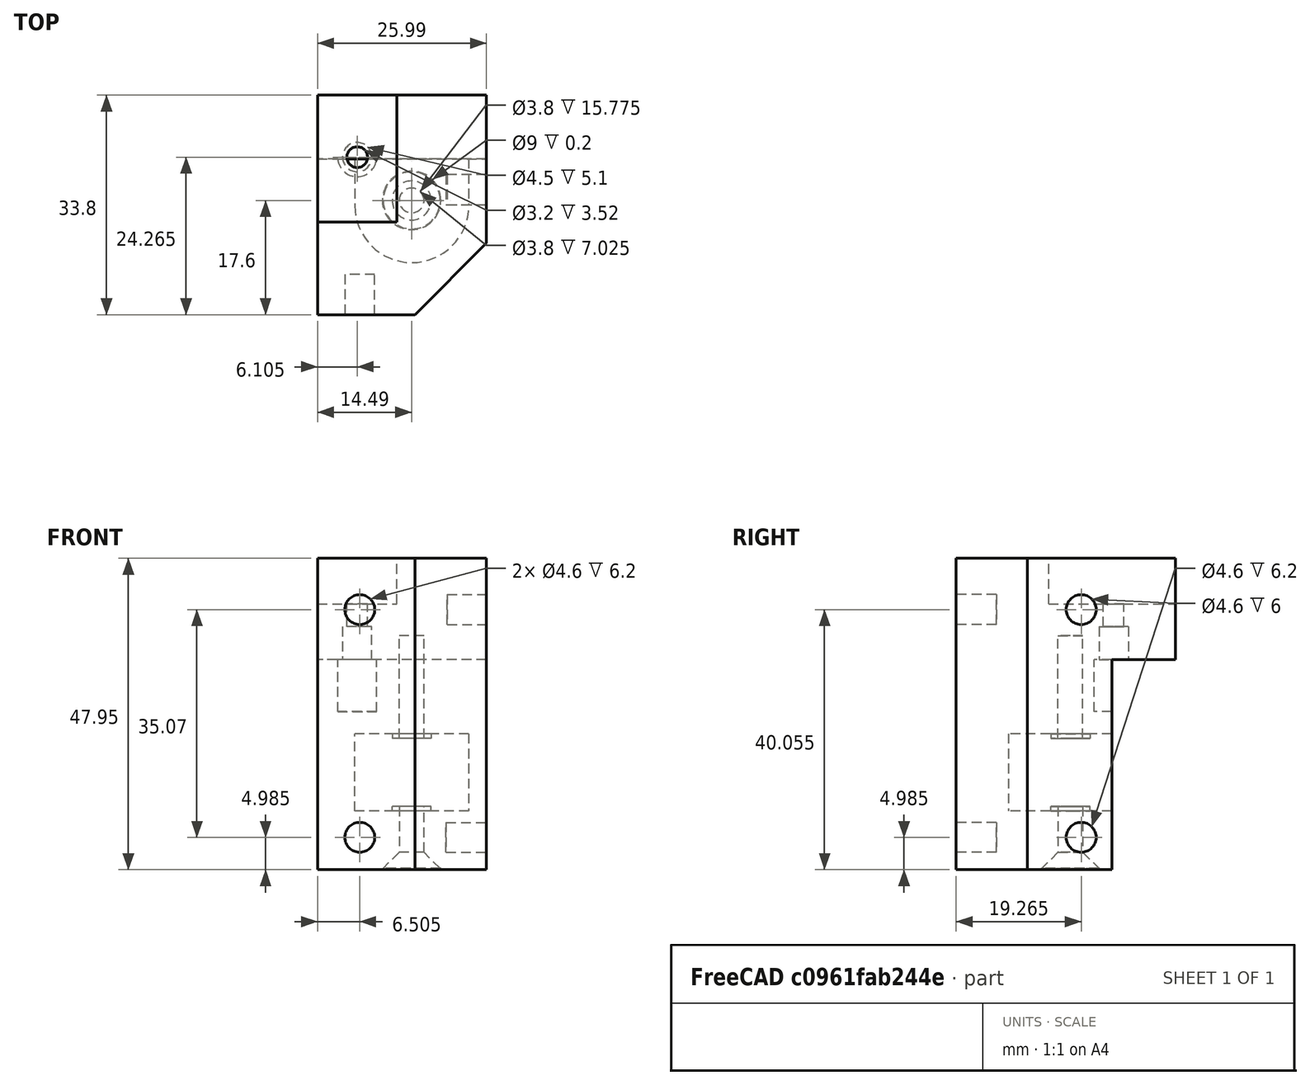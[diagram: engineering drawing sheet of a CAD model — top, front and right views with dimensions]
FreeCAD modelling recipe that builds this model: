
FCSTD DOCUMENT  (FreeCAD 1.0R38641 +468 (Git))
Label: k1_front_idler_right
License: All rights reserved
LicenseURL: https://en.wikipedia.org/wiki/All_rights_reserved
objects: PartDesign::Pad×2, PartDesign::Pocket×2, Part::Feature×1, PartDesign::FeatureBase×1, App::Link×1, PartDesign::Body×1, App::Part×1
note: 16 computed .brp shape members not serialized (recipe doc carries the construction recipe); baked Part::Feature solids carry a one-line shape summary decoded from their .brp
EXTERNAL_REF file=cad_powge_pulley.FCStd obj=Part

FEATURE [Part::Feature] Part__Feature  label="step"
  shape: bbox 25.99 x 33.8 x 47.95 mm, 40 faces (baked)
FEATURE [PartDesign::FeatureBase] BaseFeature
  BaseFeature = -> Part__Feature
  Suppressed = false
FEATURE [App::Link] Link  label="cad_powge_pulley"
  LinkPlacement = pos=(-11.5,17.6,9.74) rot=(0,0,1;0rad)
  LinkedObject = -> <external cad_powge_pulley.FCStd>#Part
  Placement = pos=(-11.5,17.6,9.74) rot=(0,0,1;0rad)
FEATURE [PartDesign::Pad] Pad
  BaseFeature = -> BaseFeature
  Direction = (0,0,-1)
  Length = 0.7
  Length2 = 10
  Profile = -> BaseFeature [Face35]
  Refine = true
  Suppressed = false
  Type = 0
FEATURE [PartDesign::Pocket] Pocket
  BaseFeature = -> Pad
  Direction = (0,0,-1)
  Length = 0.7
  Length2 = 5
  Profile = -> Pad [Face30]
  Refine = true
  Suppressed = false
  Type = 0
FEATURE [PartDesign::Pad] Pad001
  BaseFeature = -> Pocket
  Direction = (0,0,-1)
  Length = 0.7
  Length2 = 10
  Profile = -> Pocket [Face5]
  Refine = true
  Suppressed = false
  Type = 0
FEATURE [PartDesign::Pocket] Pocket001
  BaseFeature = -> Pad001
  Direction = (0,0,-1)
  Length = 0.7
  Length2 = 5
  Profile = -> Pad001 [Face11]
  Refine = true
  Suppressed = false
  Type = 0
FEATURE [PartDesign::Body] Body  label="k1_front_idler_right"
  AllowCompound = false
  BaseFeature = -> Part__Feature
  Group = -> [BaseFeature,Pad,Pocket,Pad001,Pocket001]
  Origin = -> Origin
  Tip = -> Pocket001
FEATURE [App::Part] Part  label="k1_front_idler_right_part"
  Group = -> [Body,Link]
  Origin = -> Origin001

RESOLVED EXTERNAL PARTS (link-assembly join: the EXTERNAL_REF files above that resolve inside this repo's crawl, each included once):
---- part cad_powge_pulley.FCStd = doc fcstd_d49da9a9e340 ----
FCSTD DOCUMENT  (FreeCAD 1.0R38641 +468 (Git))
Label: cad_powge_pulley
License: All rights reserved
LicenseURL: https://en.wikipedia.org/wiki/All_rights_reserved
objects: Sketcher::SketchObject×1, PartDesign::Revolution×1, PartDesign::Body×1, App::Part×1
note: 6 computed .brp shape members not serialized (recipe doc carries the construction recipe); baked Part::Feature solids carry a one-line shape summary decoded from their .brp

FEATURE [Sketcher::SketchObject] Sketch
  ArcFitTolerance = 1e-06
  AttachmentSupport = -> [XZ_Plane]
  FullyConstrained = true
  MakeInternals = false
  MapMode = 5
  Placement = pos=(0,0,0) rot=(1,0,0;1.5708rad)
  sketch-geometry (8):
    g0: LineSegment StartX=6.1 StartY=9.3 StartZ=0 EndX=6.1 EndY=1.2 EndZ=0
    g1: LineSegment StartX=6.1 StartY=1.2 StartZ=0 EndX=8 EndY=1.2 EndZ=0
    g2: LineSegment StartX=8 StartY=1.2 StartZ=0 EndX=8 EndY=0 EndZ=0
    g3: LineSegment StartX=8 StartY=0 StartZ=0 EndX=2 EndY=0 EndZ=0
    g4: LineSegment StartX=2 StartY=0 StartZ=0 EndX=2 EndY=10.5 EndZ=0
    g5: LineSegment StartX=2 StartY=10.5 StartZ=0 EndX=8 EndY=10.5 EndZ=0
    g6: LineSegment StartX=8 StartY=10.5 StartZ=0 EndX=8 EndY=9.3 EndZ=0
    g7: LineSegment StartX=8 StartY=9.3 StartZ=0 EndX=6.1 EndY=9.3 EndZ=0
  constraints (24):
    c: Vertical(g0)
    c: Coincident(g1,g0)
    c: Horizontal(g1)
    c: Coincident(g2,g1)
    c: PointOnObject(g2,g-1)
    c: Vertical(g2)
    c: Coincident(g3,g2)
    c: PointOnObject(g3,g-1)
    c: Coincident(g4,g3)
    c: Vertical(g4)
    c: Coincident(g5,g4)
    c: Horizontal(g5)
    c: Coincident(g6,g5)
    c: Vertical(g6)
    c: Coincident(g7,g6)
    c: Horizontal(g7)
    c: Coincident(g0,g7)
    c: Equal(g5,g3)
    c: Equal(g6,g2)
    c: Distance(g4,g-2) = 2
    c: Distance(g5,g-2) = 8
    c: DistanceY(g0,g0) = 8.1
    c: DistanceY(g4,g4) = 10.5
    c: Distance(g0,g-2) = 6.1
FEATURE [PartDesign::Revolution] Revolution
  Angle = 360
  Angle2 = 60
  Axis = (0,2e-16,1)
  Base = (0,0,0)
  Placement = pos=(0,0,0) rot=(1,0,0;1.5708rad)
  Profile = -> Sketch
  ReferenceAxis = -> Sketch [V_Axis]
  Refine = true
  Reversed = true
  Suppressed = false
  Type = 0
FEATURE [PartDesign::Body] Body  label="powge_pulley"
  AllowCompound = false
  Group = -> [Sketch,Revolution]
  Origin = -> Origin
  Tip = -> Revolution
FEATURE [App::Part] Part  label="powge_pulley_part"
  Group = -> [Body]
  Origin = -> Origin001
